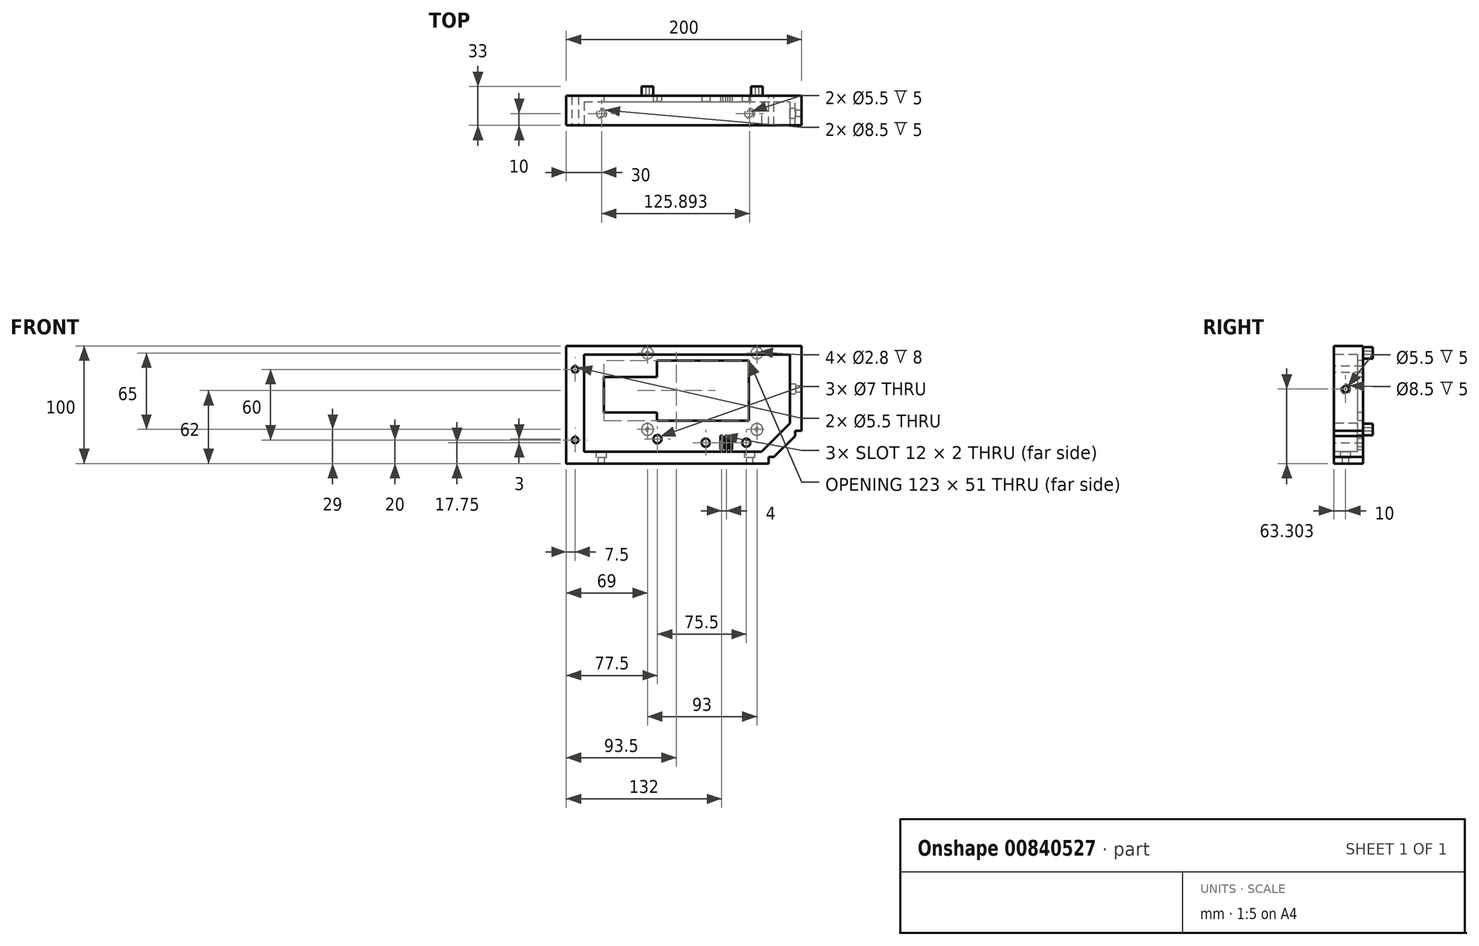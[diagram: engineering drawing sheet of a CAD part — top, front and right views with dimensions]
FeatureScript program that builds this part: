
annotation { "Feature Type Name" : "Feature", "Feature Type Description" : "" }
export const myFeature = defineFeature(function(context is Context, id is Id, definition is map)
    precondition{}
    {
        {
            var Q0;
            Q0=qCreatedBy(makeId("Front.planeOp"),FACE);
            var sketch = newSketch(context, id + "F0", { "sketchPlane" : qUnion([Q0])});
            skLineSegment(sketch, "E0.bottom", {"start": v(0, 0) * mm, "end": v(200, 0) * mm});
            skLineSegment(sketch, "E0.top", {"start": v(0, -100) * mm, "end": v(172, -100) * mm});
            skLineSegment(sketch, "E0.left", {"start": v(0, 0) * mm, "end": v(0, -100) * mm});
            skLineSegment(sketch, "E0.right", {"start": v(200, 0) * mm, "end": v(200, -72) * mm});
            skLineSegment(sketch, "E1", {"start": v(172, -100) * mm, "end": v(172, -94.5) * mm});
            skLineSegment(sketch, "E2", {"start": v(172, -94.5) * mm, "end": v(176.5, -94.5) * mm});
            skLineSegment(sketch, "E3", {"start": v(176.5, -94.5) * mm, "end": v(194.5, -76.5) * mm});
            skLineSegment(sketch, "E4", {"start": v(194.5, -76.5) * mm, "end": v(194.5, -72) * mm});
            skLineSegment(sketch, "E5", {"start": v(194.5, -72) * mm, "end": v(200, -72) * mm});
            skSolve(sketch);
        }
        {
            var Q0;
            Q0 = qSketchRegion(id + "F0", true);
            extrude(context, id + "F1", {"entities" : qUnion([Q0]), "depth" : 25 * mm, "offsetDistance" : 25 * mm});
        }
        {
            var Q0;
            Q0=makeQuery(id+"F1.opExtrude","CAP_FACE",FACE,{"disambiguationData":[OSD([sQuery(id+"F0.wireOp",EDGE,"E0.bottom"),sQuery(id+"F0.wireOp",EDGE,"E0.top"),sQuery(id+"F0.wireOp",EDGE,"E0.left"),sQuery(id+"F0.wireOp",EDGE,"E0.right"),sQuery(id+"F0.wireOp",EDGE,"E1"),sQuery(id+"F0.wireOp",EDGE,"E2"),sQuery(id+"F0.wireOp",EDGE,"E3"),sQuery(id+"F0.wireOp",EDGE,"E4"),sQuery(id+"F0.wireOp",EDGE,"E5")])],"isStart":false});
            var sketch = newSketch(context, id + "F2", { "sketchPlane" : qUnion([Q0])});
            skLineSegment(sketch, "E6.bottom", {"start": v(15, -7.5) * mm, "end": v(190, -7.5) * mm});
            skLineSegment(sketch, "E6.top", {"start": v(15, -90) * mm, "end": v(165.9, -90) * mm});
            skLineSegment(sketch, "E6.left", {"start": v(15, -7.5) * mm, "end": v(15, -90) * mm});
            skLineSegment(sketch, "E7", {"start": v(172, -94.5) * mm, "end": v(194.5, -72) * mm, "construction": true});
            skLineSegment(sketch, "E8.0", {"start": v(165.9, -90) * mm, "end": v(190, -65.9) * mm});
            skLineSegment(sketch, "E9.0", {"start": v(190, -7.5) * mm, "end": v(190, -65.9) * mm});
            skSolve(sketch);
        }
        {
            var Q0;
            Q0 = qSketchRegion(id + "F2", true);
            extrude(context, id + "F3", {"entities" : qUnion([Q0]), "operationType" : NewBodyOperationType.REMOVE, "oppositeDirection" : true, "depth" : 20 * mm, "offsetDistance" : 25 * mm});
        }
        {
            var Q0;
            Q0=makeQuery(id+"F3.boolean.opBoolean","COPY",FACE,{"derivedFrom":makeQuery(id+"F3.opExtrude","CAP_FACE",FACE,{"disambiguationData":[OSD([sQuery(id+"F2.wireOp",EDGE,"E6.bottom"),sQuery(id+"F2.wireOp",EDGE,"E6.top"),sQuery(id+"F2.wireOp",EDGE,"E6.left"),sQuery(id+"F2.wireOp",EDGE,"E6.right")])],"isStart":false})});
            var sketch = newSketch(context, id + "F4", { "sketchPlane" : qUnion([Q0])});
            skLineSegment(sketch, "E10.bottom", {"start": v(77, -12.5) * mm, "end": v(155, -12.5) * mm});
            skLineSegment(sketch, "E10.top", {"start": v(77, -63.5) * mm, "end": v(155, -63.5) * mm});
            skLineSegment(sketch, "E10.left", {"start": v(77, -12.5) * mm, "end": v(77, -26.5) * mm});
            skLineSegment(sketch, "E10.right", {"start": v(155, -12.5) * mm, "end": v(155, -63.5) * mm});
            skCircle(sketch, "E11", {"center": v(153, -82.25) * mm, "radius": 3.5 * mm});
            skLineSegment(sketch, "E12", {"start": v(153, -82.25) * mm, "end": v(118.5, -82.25) * mm, "construction": true});
            skCircle(sketch, "E13", {"center": v(118.5, -82.25) * mm, "radius": 3.5 * mm});
            skArc(sketch, "E14", {"start": v(133, -77.25) * mm, "mid": v(132, -76.25) * mm, "end": v(131, -77.25) * mm});
            skLineSegment(sketch, "E15", {"start": v(133, -77.25) * mm, "end": v(133, -82.25) * mm});
            skLineSegment(sketch, "E16", {"start": v(131, -77.25) * mm, "end": v(131, -82.25) * mm});
            skLineSegment(sketch, "E17.1.0.0", {"start": v(135, -77.25) * mm, "end": v(135, -82.25) * mm});
            skArc(sketch, "E17.1.0.1", {"start": v(137, -77.25) * mm, "mid": v(136, -76.25) * mm, "end": v(135, -77.25) * mm});
            skLineSegment(sketch, "E17.1.0.2", {"start": v(137, -77.25) * mm, "end": v(137, -82.25) * mm});
            skLineSegment(sketch, "E17.2.0.0", {"start": v(139, -77.25) * mm, "end": v(139, -82.25) * mm});
            skArc(sketch, "E17.2.0.1", {"start": v(141, -77.25) * mm, "mid": v(140, -76.25) * mm, "end": v(139, -77.25) * mm});
            skLineSegment(sketch, "E17.2.0.2", {"start": v(141, -77.25) * mm, "end": v(141, -82.25) * mm});
            skLineSegment(sketch, "E17.direction1", {"start": v(131, -82.25) * mm, "end": v(135, -82.25) * mm, "construction": true});
            skArc(sketch, "E18.MirrorCS", {"start": v(141, -87.25) * mm, "mid": v(140, -88.25) * mm, "end": v(139, -87.25) * mm});
            skArc(sketch, "E19.MirrorCS", {"start": v(133, -87.25) * mm, "mid": v(132, -88.25) * mm, "end": v(131, -87.25) * mm});
            skLineSegment(sketch, "E20.MirrorCS", {"start": v(139, -87.25) * mm, "end": v(139, -82.25) * mm});
            skLineSegment(sketch, "E21.MirrorCS", {"start": v(137, -87.25) * mm, "end": v(137, -82.25) * mm});
            skLineSegment(sketch, "E22.MirrorCS", {"start": v(133, -87.25) * mm, "end": v(133, -82.25) * mm});
            skLineSegment(sketch, "E23.MirrorCS", {"start": v(135, -87.25) * mm, "end": v(135, -82.25) * mm});
            skLineSegment(sketch, "E24.MirrorCS", {"start": v(141, -87.25) * mm, "end": v(141, -82.25) * mm});
            skLineSegment(sketch, "E25.MirrorCS", {"start": v(131, -87.25) * mm, "end": v(131, -82.25) * mm});
            skArc(sketch, "E26.MirrorCS", {"start": v(137, -87.25) * mm, "mid": v(136, -88.25) * mm, "end": v(135, -87.25) * mm});
            skLineSegment(sketch, "E27", {"start": v(118.5, -82.25) * mm, "end": v(77.5, -79.25) * mm, "construction": true});
            skCircle(sketch, "E28", {"center": v(77.5, -79.25) * mm, "radius": 3.5 * mm});
            skLineSegment(sketch, "E29", {"start": v(77, -26.5) * mm, "end": v(32, -26.5) * mm});
            skLineSegment(sketch, "E30", {"start": v(32, -26.5) * mm, "end": v(32, -56.5) * mm});
            skLineSegment(sketch, "E31", {"start": v(32, -56.5) * mm, "end": v(77, -56.5) * mm});
            skLineSegment(sketch, "E32.trimOffspring", {"start": v(77, -56.5) * mm, "end": v(77, -63.5) * mm});
            skSolve(sketch);
        }
        {
            var Q0;
            Q0 = qSketchRegion(id + "F4", true);
            var Q1;
            Q1=makeQuery(id+"F1.opExtrude","CAP_FACE",FACE,{"disambiguationData":[OSD([sQuery(id+"F0.wireOp",EDGE,"E0.bottom"),sQuery(id+"F0.wireOp",EDGE,"E0.top"),sQuery(id+"F0.wireOp",EDGE,"E0.left"),sQuery(id+"F0.wireOp",EDGE,"E0.right"),sQuery(id+"F0.wireOp",EDGE,"E1"),sQuery(id+"F0.wireOp",EDGE,"E2"),sQuery(id+"F0.wireOp",EDGE,"E3"),sQuery(id+"F0.wireOp",EDGE,"E4"),sQuery(id+"F0.wireOp",EDGE,"E5")])],"isStart":true});
            extrude(context, id + "F5", {"entities" : qUnion([Q0]), "operationType" : NewBodyOperationType.REMOVE, "endBound" : BoundingType.UP_TO_SURFACE, "oppositeDirection" : true, "depth" : 25 * mm, "endBoundEntityFace" : qUnion([Q1]), "offsetDistance" : 25 * mm});
        }
        {
            var Q0;
            Q0=makeQuery(id+"F1.opExtrude","CAP_FACE",FACE,{"disambiguationData":[OSD([sQuery(id+"F0.wireOp",EDGE,"E0.bottom"),sQuery(id+"F0.wireOp",EDGE,"E0.top"),sQuery(id+"F0.wireOp",EDGE,"E0.left"),sQuery(id+"F0.wireOp",EDGE,"E0.right"),sQuery(id+"F0.wireOp",EDGE,"E1"),sQuery(id+"F0.wireOp",EDGE,"E2"),sQuery(id+"F0.wireOp",EDGE,"E3"),sQuery(id+"F0.wireOp",EDGE,"E4"),sQuery(id+"F0.wireOp",EDGE,"E5")])],"isStart":true});
            var sketch = newSketch(context, id + "F6", { "sketchPlane" : qUnion([Q0])});
            skLineSegment(sketch, "E33.bottom", {"start": v(-162, -6) * mm, "end": v(-69, -6) * mm, "construction": true});
            skLineSegment(sketch, "E33.top", {"start": v(-162, -71) * mm, "end": v(-69, -71) * mm, "construction": true});
            skLineSegment(sketch, "E33.left", {"start": v(-162, -6) * mm, "end": v(-162, -71) * mm, "construction": true});
            skLineSegment(sketch, "E33.right", {"start": v(-69, -6) * mm, "end": v(-69, -71) * mm, "construction": true});
            skCircle(sketch, "E34", {"center": v(-69, -6) * mm, "radius": 5 * mm});
            skCircle(sketch, "E35", {"center": v(-162, -6) * mm, "radius": 5 * mm});
            skCircle(sketch, "E36", {"center": v(-162, -71) * mm, "radius": 5 * mm});
            skCircle(sketch, "E37", {"center": v(-69, -71) * mm, "radius": 5 * mm});
            skCircle(sketch, "E38", {"center": v(-69, -6) * mm, "radius": 1.4 * mm});
            skCircle(sketch, "E39", {"center": v(-162, -6) * mm, "radius": 1.4 * mm});
            skCircle(sketch, "E40", {"center": v(-162, -71) * mm, "radius": 1.4 * mm});
            skCircle(sketch, "E41", {"center": v(-69, -71) * mm, "radius": 1.4 * mm});
            skSolve(sketch);
        }
        {
            var Q0;
            Q0 = qSketchRegion(id + "F6", true);
            extrude(context, id + "F7", {"entities" : qUnion([Q0]), "operationType" : NewBodyOperationType.ADD, "depth" : 8 * mm, "offsetDistance" : 25 * mm});
        }
        {
            var Q0;
            Q0=makeQuery(id+"F3.boolean.opBoolean","COPY",FACE,{"derivedFrom":makeQuery(id+"F3.opExtrude","SWEPT_FACE",FACE,{"disambiguationData":[OSD([sQuery(id+"F2.wireOp",EDGE,"E9.0")])]})});
            var sketch = newSketch(context, id + "F8", { "sketchPlane" : qUnion([Q0])});
            skLineSegment(sketch, "E42", {"start": v(5, -65.9) * mm, "end": v(25, -7.5) * mm, "construction": true});
            skCircle(sketch, "E43", {"center": v(15, -36.7) * mm, "radius": 2.75 * mm});
            skSolve(sketch);
        }
        {
            var Q0;
            Q0 = qSketchRegion(id + "F8", true);
            var Q1;
            Q1=makeQuery(id+"F1.opExtrude","SWEPT_FACE",FACE,{"disambiguationData":[OSD([sQuery(id+"F0.wireOp",EDGE,"E0.right")])]});
            extrude(context, id + "F9", {"entities" : qUnion([Q0]), "operationType" : NewBodyOperationType.REMOVE, "endBound" : BoundingType.UP_TO_SURFACE, "oppositeDirection" : true, "depth" : 25 * mm, "endBoundEntityFace" : qUnion([Q1]), "offsetDistance" : 25 * mm});
        }
        {
            var Q0;
            Q0=makeQuery(id+"F3.boolean.opBoolean","COPY",FACE,{"derivedFrom":makeQuery(id+"F3.opExtrude","SWEPT_FACE",FACE,{"disambiguationData":[OSD([sQuery(id+"F2.wireOp",EDGE,"E9.0")])]})});
            var sketch = newSketch(context, id + "F10", { "sketchPlane" : qUnion([Q0])});
            skCircle(sketch, "E44", {"center": v(15, -36.7) * mm, "radius": 4.25 * mm});
            skSolve(sketch);
        }
        {
            var Q0;
            Q0 = qSketchRegion(id + "F10", true);
            extrude(context, id + "F11", {"entities" : qUnion([Q0]), "operationType" : NewBodyOperationType.REMOVE, "oppositeDirection" : true, "depth" : 5 * mm, "offsetDistance" : 25 * mm});
        }
        {
            var Q0;
            Q0=makeQuery(id+"F3.boolean.opBoolean","COPY",FACE,{"derivedFrom":makeQuery(id+"F3.opExtrude","SWEPT_FACE",FACE,{"disambiguationData":[OSD([sQuery(id+"F2.wireOp",EDGE,"E6.top")])]})});
            var sketch = newSketch(context, id + "F12", { "sketchPlane" : qUnion([Q0])});
            skLineSegment(sketch, "E45", {"start": v(15, -15) * mm, "end": v(30, -15) * mm, "construction": true});
            skLineSegment(sketch, "E46", {"start": v(165.9, -15) * mm, "end": v(155.9, -15) * mm, "construction": true});
            skCircle(sketch, "E47", {"center": v(30, -15) * mm, "radius": 2.75 * mm});
            skCircle(sketch, "E48", {"center": v(155.9, -15) * mm, "radius": 2.75 * mm});
            skSolve(sketch);
        }
        {
            var Q0;
            Q0 = qSketchRegion(id + "F12", true);
            var Q1;
            Q1=makeQuery(id+"F1.opExtrude","SWEPT_FACE",FACE,{"disambiguationData":[OSD([sQuery(id+"F0.wireOp",EDGE,"E0.top")])]});
            extrude(context, id + "F13", {"entities" : qUnion([Q0]), "operationType" : NewBodyOperationType.REMOVE, "endBound" : BoundingType.UP_TO_SURFACE, "oppositeDirection" : true, "depth" : 25 * mm, "endBoundEntityFace" : qUnion([Q1]), "offsetDistance" : 25 * mm});
        }
        {
            var Q0;
            Q0=makeQuery(id+"F3.boolean.opBoolean","COPY",FACE,{"derivedFrom":makeQuery(id+"F3.opExtrude","SWEPT_FACE",FACE,{"disambiguationData":[OSD([sQuery(id+"F2.wireOp",EDGE,"E6.top")])]})});
            var sketch = newSketch(context, id + "F14", { "sketchPlane" : qUnion([Q0])});
            skCircle(sketch, "E49", {"center": v(30, -15) * mm, "radius": 4.25 * mm});
            skCircle(sketch, "E50", {"center": v(155.9, -15) * mm, "radius": 4.25 * mm});
            skSolve(sketch);
        }
        {
            var Q0;
            Q0 = qSketchRegion(id + "F14", true);
            extrude(context, id + "F15", {"entities" : qUnion([Q0]), "operationType" : NewBodyOperationType.REMOVE, "oppositeDirection" : true, "depth" : 5 * mm, "offsetDistance" : 25 * mm});
        }
        {
            var Q0;
            Q0=makeQuery(id+"F1.opExtrude","CAP_FACE",FACE,{"disambiguationData":[OSD([sQuery(id+"F0.wireOp",EDGE,"E0.bottom"),sQuery(id+"F0.wireOp",EDGE,"E0.top"),sQuery(id+"F0.wireOp",EDGE,"E0.left"),sQuery(id+"F0.wireOp",EDGE,"E0.right"),sQuery(id+"F0.wireOp",EDGE,"E1"),sQuery(id+"F0.wireOp",EDGE,"E2"),sQuery(id+"F0.wireOp",EDGE,"E3"),sQuery(id+"F0.wireOp",EDGE,"E4"),sQuery(id+"F0.wireOp",EDGE,"E5")])],"isStart":false});
            var sketch = newSketch(context, id + "F16", { "sketchPlane" : qUnion([Q0])});
            skLineSegment(sketch, "E51", {"start": v(7.5, -100) * mm, "end": v(7.5, 0) * mm, "construction": true});
            skCircle(sketch, "E52", {"center": v(7.5, -20) * mm, "radius": 2.75 * mm});
            skCircle(sketch, "E53", {"center": v(7.5, -80) * mm, "radius": 2.75 * mm});
            skSolve(sketch);
        }
        {
            var Q0;
            Q0 = qSketchRegion(id + "F16", true);
            var Q1;
            {var subQ0=sQuery(id+"F0.wireOp",EDGE,"E0.bottom");var subQ1=sQuery(id+"F0.wireOp",EDGE,"E0.left");var subQ2=sQuery(id+"F0.wireOp",EDGE,"E0.top");var subQ3=sQuery(id+"F0.wireOp",EDGE,"E0.right");var subQ4=sQuery(id+"F0.wireOp",EDGE,"E1");var subQ5=sQuery(id+"F0.wireOp",EDGE,"E2");var subQ6=sQuery(id+"F0.wireOp",EDGE,"E3");var subQ7=sQuery(id+"F0.wireOp",EDGE,"E4");var subQ8=sQuery(id+"F0.wireOp",EDGE,"E5");Q1=makeQuery(id+"F7.boolean.opBoolean","SPLIT",FACE,{"disambiguationData":[TD([makeQuery(id+"F1.opExtrude","SWEPT_FACE",FACE,{"disambiguationData":[OSD([subQ0])]})])],"derivedFrom":makeQuery(id+"F1.opExtrude","CAP_FACE",FACE,{"disambiguationData":[OSD([subQ0,subQ2,subQ1,subQ3,subQ4,subQ5,subQ6,subQ7,subQ8])],"isStart":true})});}
            extrude(context, id + "F17", {"entities" : qUnion([Q0]), "operationType" : NewBodyOperationType.REMOVE, "endBound" : BoundingType.UP_TO_SURFACE, "oppositeDirection" : true, "depth" : 25 * mm, "endBoundEntityFace" : qUnion([Q1]), "offsetDistance" : 25 * mm});
        }
    });
